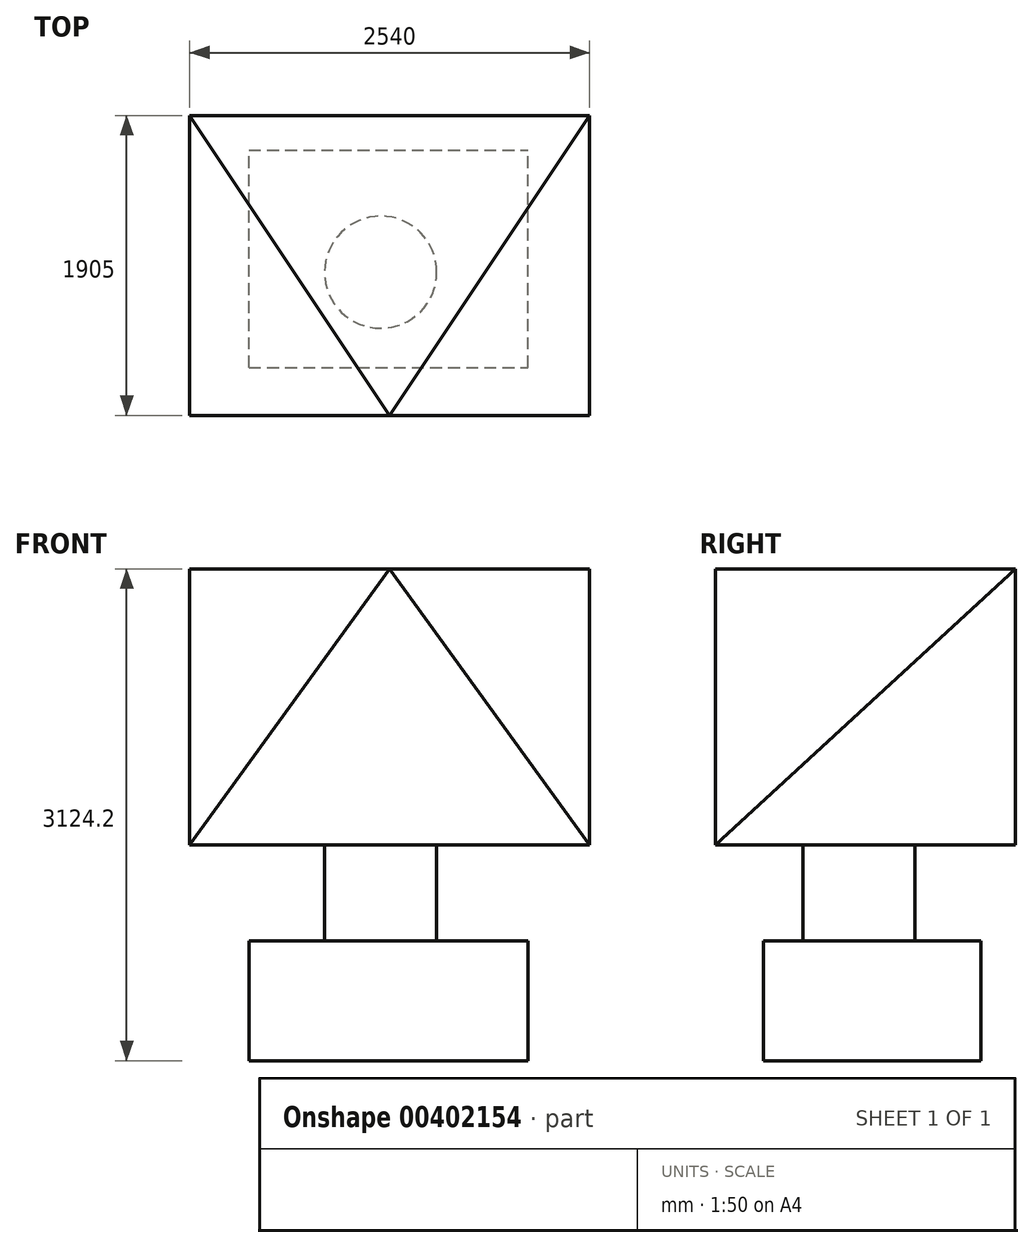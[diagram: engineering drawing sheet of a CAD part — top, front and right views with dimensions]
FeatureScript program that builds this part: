
annotation { "Feature Type Name" : "Feature", "Feature Type Description" : "" }
export const myFeature = defineFeature(function(context is Context, id is Id, definition is map)
    precondition{}
    {
        {
            var Q0;
            Q0=qCreatedBy(makeId("Front.planeOp"),FACE);
            var sketch = newSketch(context, id + "F0", { "sketchPlane" : qUnion([Q0])});
            skLineSegment(sketch, "E0", {"start": v(0, 0) * mm, "end": v(2540, 0) * mm});
            skLineSegment(sketch, "E1", {"start": v(2540, 0) * mm, "end": v(2540, -1752.6) * mm});
            skLineSegment(sketch, "E2", {"start": v(2540, -1752.6) * mm, "end": v(0, -1752.6) * mm});
            skLineSegment(sketch, "E3", {"start": v(0, -1752.6) * mm, "end": v(0, 0) * mm});
            skSolve(sketch);
        }
        {
            var Q0;
            Q0=makeQuery(id+"F0.imprint","IMPRINT",FACE,{"disambiguationData":[TD([[makeQuery(id+"F0.imprint","IMPRINT",EDGE,{"derivedFrom":sQuery(id+"F0.wireOp",EDGE,"E0")}),-1.0]])]});
            extrude(context, id + "F1", {"entities" : qUnion([Q0]), "depth" : 1905 * mm});
        }
        {
            var Q0;
            Q0=makeQuery(id+"F1.opExtrude","SWEPT_FACE",FACE,{"disambiguationData":[OSD([sQuery(id+"F0.wireOp",EDGE,"E1")])]});
            var sketch = newSketch(context, id + "F2", { "sketchPlane" : qUnion([Q0])});
            skLineSegment(sketch, "E4", {"start": v(0, 0) * mm, "end": v(-1905, -1752.6) * mm});
            skLineSegment(sketch, "E5", {"start": v(-1905, 0) * mm, "end": v(-1422.4, 0) * mm});
            skLineSegment(sketch, "E6", {"start": v(-1422.4, 0) * mm, "end": v(-1422.4, -482.6) * mm});
            skLineSegment(sketch, "E7", {"start": v(-1422.4, -482.6) * mm, "end": v(-609.6, -482.6) * mm});
            skLineSegment(sketch, "E8", {"start": v(-609.6, -482.6) * mm, "end": v(-609.6, 0) * mm});
            skLineSegment(sketch, "E9", {"start": v(-609.6, 0) * mm, "end": v(0, 0) * mm});
            skLineSegment(sketch, "E10", {"start": v(-1905, 0) * mm, "end": v(-1905, -1752.6) * mm});
            skSolve(sketch);
        }
        {
            var Q0;
            Q0=makeQuery(id+"F1.opExtrude","CAP_FACE",FACE,{"disambiguationData":[OSD([sQuery(id+"F0.wireOp",EDGE,"E0"),sQuery(id+"F0.wireOp",EDGE,"E1"),sQuery(id+"F0.wireOp",EDGE,"E2"),sQuery(id+"F0.wireOp",EDGE,"E3")])],"isStart":false});
            var sketch = newSketch(context, id + "F3", { "sketchPlane" : qUnion([Q0])});
            skLineSegment(sketch, "E11", {"start": v(1270, 0) * mm, "end": v(2540, -1752.6) * mm});
            skSolve(sketch);
        }
        {
            var Q0;
            Q0=sQuery(id+"F3.wireOp",VERTEX,"E11.start");
            var Q1;
            Q1=sQuery(id+"F2.wireOp",VERTEX,"E9.end");
            var Q2;
            Q2=sQuery(id+"F3.wireOp",VERTEX,"E11.end");
            cPlane(context, id + "F4", {"entities" : qUnion([Q0, Q1, Q2]), "cplaneType" : CPlaneType.THREE_POINT, "offset" : 152.4 * mm, "width" : 152.4 * mm, "height" : 152.4 * mm});
        }
        {
            var Q0;
            Q0=qCreatedBy(id+"F4.planeOp",FACE);
            var sketch = newSketch(context, id + "F5", { "sketchPlane" : qUnion([Q0])});
            skLineSegment(sketch, "E12", {"start": v(-3737.09, 250.38) * mm, "end": v(-2471.14, -4877.21) * mm});
            skLineSegment(sketch, "E13", {"start": v(-2471.14, -4877.21) * mm, "end": v(9797.3, -2905.45) * mm});
            skLineSegment(sketch, "E14", {"start": v(9797.3, -2905.45) * mm, "end": v(3353.72, 2692.03) * mm});
            skLineSegment(sketch, "E15", {"start": v(3353.72, 2692.03) * mm, "end": v(-3737.09, 250.38) * mm});
            skSolve(sketch);
        }
        {
            var Q0;
            Q0=makeQuery(id+"F5.imprint","IMPRINT",FACE,{"disambiguationData":[TD([[makeQuery(id+"F5.imprint","IMPRINT",EDGE,{"derivedFrom":sQuery(id+"F5.wireOp",EDGE,"E12")}),1.0]])]});
            extrude(context, id + "F6", {"entities" : qUnion([Q0]), "operationType" : NewBodyOperationType.REMOVE, "depth" : 2540 * mm});
        }
        {
            var Q0;
            Q0=makeQuery(id+"F1.opExtrude","CAP_VERTEX",VERTEX,{"disambiguationData":[OSD([sQuery(id+"F0.wireOp",EDGE,"E0"),sQuery(id+"F0.wireOp",EDGE,"E3")])],"isStart":true});
            var Q1;
            Q1=sQuery(id+"F3.wireOp",VERTEX,"E11.start");
            var Q2;
            Q2=makeQuery(id+"F1.opExtrude","CAP_VERTEX",VERTEX,{"disambiguationData":[OSD([sQuery(id+"F0.wireOp",EDGE,"E2"),sQuery(id+"F0.wireOp",EDGE,"E3")])],"isStart":false});
            cPlane(context, id + "F7", {"entities" : qUnion([Q0, Q1, Q2]), "cplaneType" : CPlaneType.THREE_POINT, "offset" : 152.4 * mm, "width" : 152.4 * mm, "height" : 152.4 * mm});
        }
        {
            var Q0;
            Q0=qCreatedBy(id+"F7.planeOp",FACE);
            var sketch = newSketch(context, id + "F8", { "sketchPlane" : qUnion([Q0])});
            skLineSegment(sketch, "E16", {"start": v(-1106.9, 0) * mm, "end": v(6334.9, 2345.3) * mm});
            skLineSegment(sketch, "E17", {"start": v(6334.9, 2345.3) * mm, "end": v(8031.7, -2892.8) * mm});
            skLineSegment(sketch, "E18", {"start": v(8031.7, -2892.8) * mm, "end": v(464.38, -2554.35) * mm});
            skLineSegment(sketch, "E19", {"start": v(464.38, -2554.35) * mm, "end": v(-1106.9, 0) * mm});
            skSolve(sketch);
        }
        {
            var Q0;
            Q0=makeQuery(id+"F8.imprint","IMPRINT",FACE,{"disambiguationData":[TD([[makeQuery(id+"F8.imprint","IMPRINT",EDGE,{"derivedFrom":sQuery(id+"F8.wireOp",EDGE,"E16")}),-1.0]])]});
            extrude(context, id + "F9", {"entities" : qUnion([Q0]), "operationType" : NewBodyOperationType.REMOVE, "depth" : 2540 * mm});
        }
        {
            var Q0;
            Q0=makeQuery(id+"F1.opExtrude","SWEPT_FACE",FACE,{"disambiguationData":[OSD([sQuery(id+"F0.wireOp",EDGE,"E2")])]});
            var sketch = newSketch(context, id + "F10", { "sketchPlane" : qUnion([Q0])});
            skCircle(sketch, "E20", {"center": v(1212.04, 995.97) * mm, "radius": 356.21 * mm});
            skSolve(sketch);
        }
        {
            var Q0;
            Q0 = qSketchRegion(id + "F10", true);
            extrude(context, id + "F11", {"entities" : qUnion([Q0]), "operationType" : NewBodyOperationType.ADD, "depth" : 609.6 * mm});
        }
        {
            var Q0;
            Q0=makeQuery(id+"F11.opExtrude","CAP_FACE",FACE,{"disambiguationData":[OSD([sQuery(id+"F10.wireOp",EDGE,"E20")])],"isStart":false});
            var sketch = newSketch(context, id + "F12", { "sketchPlane" : qUnion([Q0])});
            skLineSegment(sketch, "E21.bottom", {"start": v(376.02, 1600.27) * mm, "end": v(2148.03, 1600.27) * mm});
            skLineSegment(sketch, "E21.top", {"start": v(376.02, 219.01) * mm, "end": v(2148.03, 219.01) * mm});
            skLineSegment(sketch, "E21.left", {"start": v(376.02, 1600.27) * mm, "end": v(376.02, 219.01) * mm});
            skLineSegment(sketch, "E21.right", {"start": v(2148.03, 1600.27) * mm, "end": v(2148.03, 219.01) * mm});
            skSolve(sketch);
        }
        {
            var Q0;
            Q0 = qSketchRegion(id + "F12", true);
            extrude(context, id + "F13", {"entities" : qUnion([Q0]), "operationType" : NewBodyOperationType.ADD, "depth" : 762 * mm});
        }
    });
